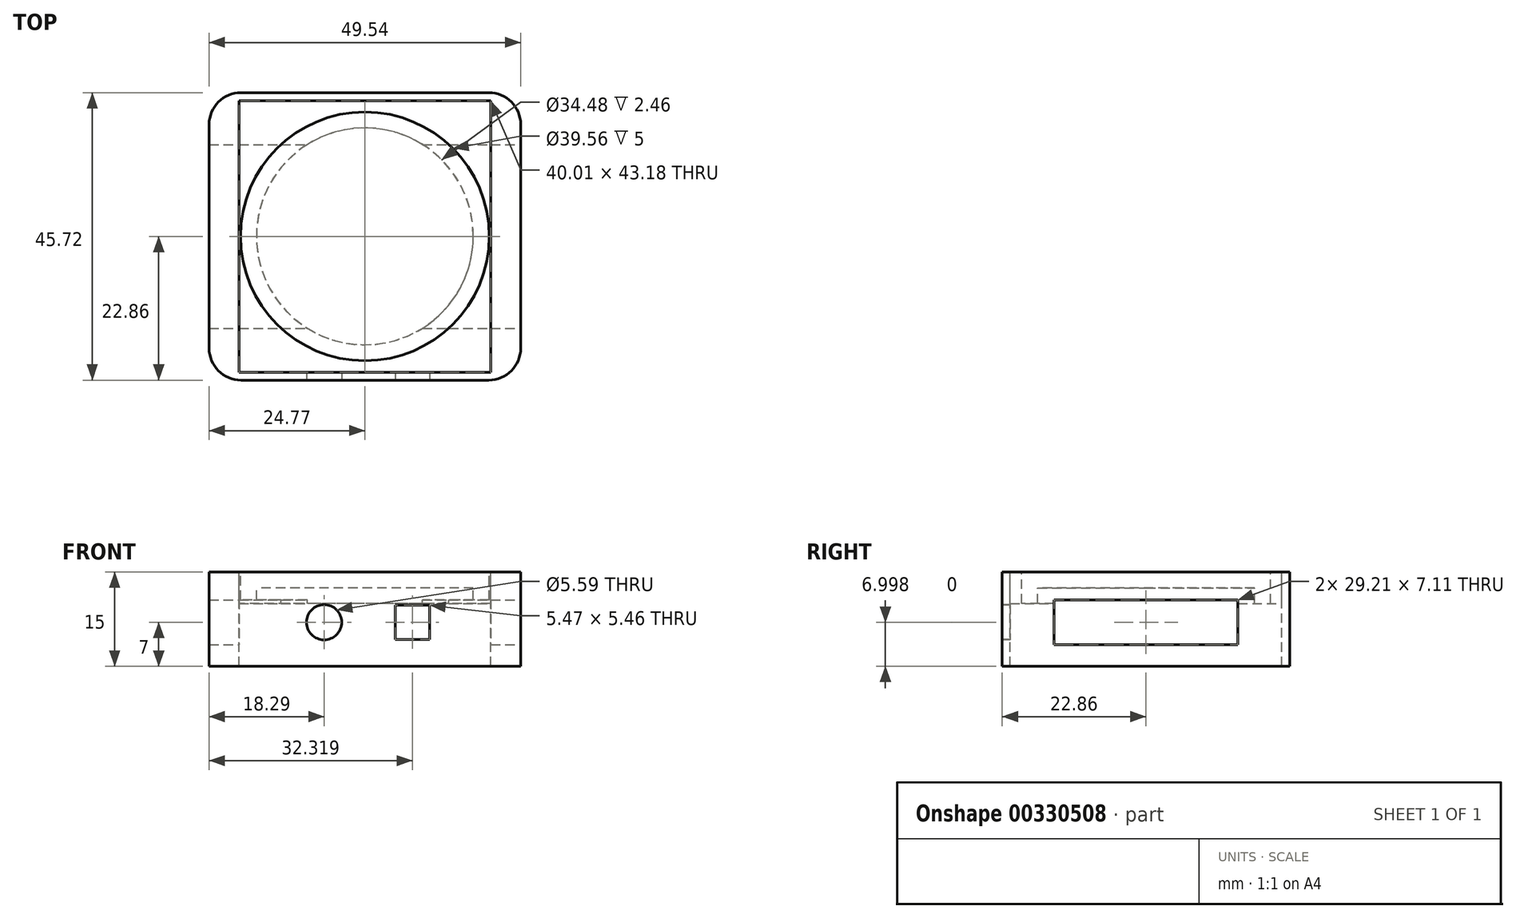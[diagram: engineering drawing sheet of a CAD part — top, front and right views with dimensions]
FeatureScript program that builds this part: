
annotation { "Feature Type Name" : "Feature", "Feature Type Description" : "" }
export const myFeature = defineFeature(function(context is Context, id is Id, definition is map)
    precondition{}
    {
        {
            var Q0;
            Q0=qCreatedBy(makeId("Top.planeOp"),FACE);
            var sketch = newSketch(context, id + "F0", { "sketchPlane" : qUnion([Q0])});
            skLineSegment(sketch, "E0.bottom", {"start": v(20, -21.59) * mm, "end": v(-20, -21.6) * mm});
            skLineSegment(sketch, "E0.top", {"start": v(20, 21.6) * mm, "end": v(-20, 21.59) * mm});
            skLineSegment(sketch, "E0.left", {"start": v(20, -21.59) * mm, "end": v(20, 21.6) * mm});
            skLineSegment(sketch, "E0.right", {"start": v(-20, -21.6) * mm, "end": v(-20, 21.59) * mm});
            skPoint(sketch, "E0.middle", {"position": v(0, 0) * mm});
            skCircle(sketch, "E1", {"center": v(0, 0) * mm, "radius": 19.78 * mm});
            skLineSegment(sketch, "E2.bottom", {"start": v(24.77, -22.86) * mm, "end": v(-24.77, -22.86) * mm});
            skLineSegment(sketch, "E2.top", {"start": v(24.77, 22.86) * mm, "end": v(-24.77, 22.86) * mm});
            skLineSegment(sketch, "E2.left", {"start": v(24.77, -22.86) * mm, "end": v(24.77, 22.86) * mm});
            skLineSegment(sketch, "E2.right", {"start": v(-24.77, -22.86) * mm, "end": v(-24.77, 22.86) * mm});
            skSolve(sketch);
        }
        {
            var Q0;
            Q0=makeQuery(id+"F0.imprint","IMPRINT",FACE,{"disambiguationData":[TD([[makeQuery(id+"F0.imprint","IMPRINT",EDGE,{"derivedFrom":sQuery(id+"F0.wireOp",EDGE,"E0.bottom")}),-1.0]])]});
            extrude(context, id + "F1", {"entities" : qUnion([Q0]), "oppositeDirection" : true, "depth" : 5 * mm});
        }
        {
            var Q0;
            Q0=qCreatedBy(makeId("Top.planeOp"),FACE);
            var sketch = newSketch(context, id + "F2", { "sketchPlane" : qUnion([Q0])});
            skCircle(sketch, "E3", {"center": v(0, 0) * mm, "radius": 19.78 * mm});
            skSolve(sketch);
        }
        {
            var Q0;
            Q0 = qSketchRegion(id + "F2", true);
            extrude(context, id + "F3", {"entities" : qUnion([Q0]), "oppositeDirection" : true, "depth" : 5 * mm});
        }
        {
            var Q0;
            Q0=makeQuery(id+"F3.opExtrude","CAP_FACE",FACE,{"disambiguationData":[OSD([sQuery(id+"F2.wireOp",EDGE,"E3")])],"isStart":false});
            shell(context, id + "F4", {"entities" : qUnion([Q0]), "thickness" : 2.54 * mm});
        }
        {
            var Q0;
            Q0=makeQuery(id+"F0.imprint","IMPRINT",FACE,{"disambiguationData":[TD([[makeQuery(id+"F0.imprint","IMPRINT",EDGE,{"derivedFrom":sQuery(id+"F0.wireOp",EDGE,"E0.bottom")}),1.0]])]});
            extrude(context, id + "F5", {"entities" : qUnion([Q0]), "oppositeDirection" : true, "depth" : 15 * mm});
        }
        {
            var Q0;
            Q0=makeQuery(id+"F5.opExtrude","SWEPT_EDGE",EDGE,{"disambiguationData":[OSD([sQuery(id+"F0.wireOp",EDGE,"E2.bottom"),sQuery(id+"F0.wireOp",EDGE,"E2.right")])]});
            var Q1;
            Q1=makeQuery(id+"F5.opExtrude","SWEPT_EDGE",EDGE,{"disambiguationData":[OSD([sQuery(id+"F0.wireOp",EDGE,"E2.bottom"),sQuery(id+"F0.wireOp",EDGE,"E2.left")])]});
            var Q2;
            Q2=makeQuery(id+"F5.opExtrude","SWEPT_EDGE",EDGE,{"disambiguationData":[OSD([sQuery(id+"F0.wireOp",EDGE,"E2.top"),sQuery(id+"F0.wireOp",EDGE,"E2.left")])]});
            var Q3;
            Q3=makeQuery(id+"F5.opExtrude","SWEPT_EDGE",EDGE,{"disambiguationData":[OSD([sQuery(id+"F0.wireOp",EDGE,"E2.top"),sQuery(id+"F0.wireOp",EDGE,"E2.right")])]});
            fillet(context, id + "F6", {"entities" : qUnion([Q0, Q1, Q2, Q3]), "radius" : 5.08 * mm, "tangentPropagation" : true, "allowEdgeOverflow" : false});
        }
        {
            var Q0;
            Q0=makeQuery(id+"F5.opExtrude","SWEPT_FACE",FACE,{"disambiguationData":[OSD([sQuery(id+"F0.wireOp",EDGE,"E2.bottom")])]});
            var sketch = newSketch(context, id + "F7", { "sketchPlane" : qUnion([Q0])});
            skLineSegment(sketch, "E4.bottom", {"start": v(4.81, -10.73) * mm, "end": v(10.28, -10.73) * mm});
            skLineSegment(sketch, "E4.top", {"start": v(4.81, -5.27) * mm, "end": v(10.28, -5.27) * mm});
            skLineSegment(sketch, "E4.left", {"start": v(4.81, -10.73) * mm, "end": v(4.81, -5.27) * mm});
            skLineSegment(sketch, "E4.right", {"start": v(10.28, -10.73) * mm, "end": v(10.28, -5.27) * mm});
            skPoint(sketch, "E4.middle", {"position": v(7.55, -8) * mm});
            skCircle(sketch, "E5", {"center": v(-6.48, -8) * mm, "radius": 2.8 * mm});
            skSolve(sketch);
        }
        {
            var Q0;
            Q0=makeQuery(id+"F7.imprint","IMPRINT",FACE,{"disambiguationData":[TD([[makeQuery(id+"F7.imprint","IMPRINT",EDGE,{"derivedFrom":sQuery(id+"F7.wireOp",EDGE,"E4.bottom")}),1.0]])]});
            var Q1;
            Q1=makeQuery(id+"F7.imprint","IMPRINT",FACE,{"disambiguationData":[TD([[makeQuery(id+"F7.imprint","IMPRINT",EDGE,{"derivedFrom":sQuery(id+"F7.wireOp",EDGE,"E5")}),1.0]])]});
            extrude(context, id + "F8", {"entities" : qUnion([Q0, Q1]), "operationType" : NewBodyOperationType.REMOVE, "oppositeDirection" : true, "depth" : 16.9 * mm});
        }
        {
            var Q0;
            Q0=makeQuery(id+"F5.opExtrude","SWEPT_FACE",FACE,{"disambiguationData":[OSD([sQuery(id+"F0.wireOp",EDGE,"E2.left")])]});
            var sketch = newSketch(context, id + "F9", { "sketchPlane" : qUnion([Q0])});
            skLineSegment(sketch, "E6.bottom", {"start": v(14.6, -4.45) * mm, "end": v(-14.6, -4.45) * mm});
            skLineSegment(sketch, "E6.top", {"start": v(14.6, -11.56) * mm, "end": v(-14.6, -11.56) * mm});
            skLineSegment(sketch, "E6.left", {"start": v(14.6, -4.45) * mm, "end": v(14.6, -11.56) * mm});
            skLineSegment(sketch, "E6.right", {"start": v(-14.6, -4.45) * mm, "end": v(-14.6, -11.56) * mm});
            skPoint(sketch, "E6.middle", {"position": v(0, -8) * mm});
            skSolve(sketch);
        }
        {
            var Q0;
            Q0=makeQuery(id+"F9.imprint","IMPRINT",FACE,{"disambiguationData":[TD([[makeQuery(id+"F9.imprint","IMPRINT",EDGE,{"derivedFrom":sQuery(id+"F9.wireOp",EDGE,"E6.bottom")}),1.0]])]});
            extrude(context, id + "F10", {"entities" : qUnion([Q0]), "operationType" : NewBodyOperationType.REMOVE, "oppositeDirection" : true, "depth" : 55.63 * mm});
        }
    });
